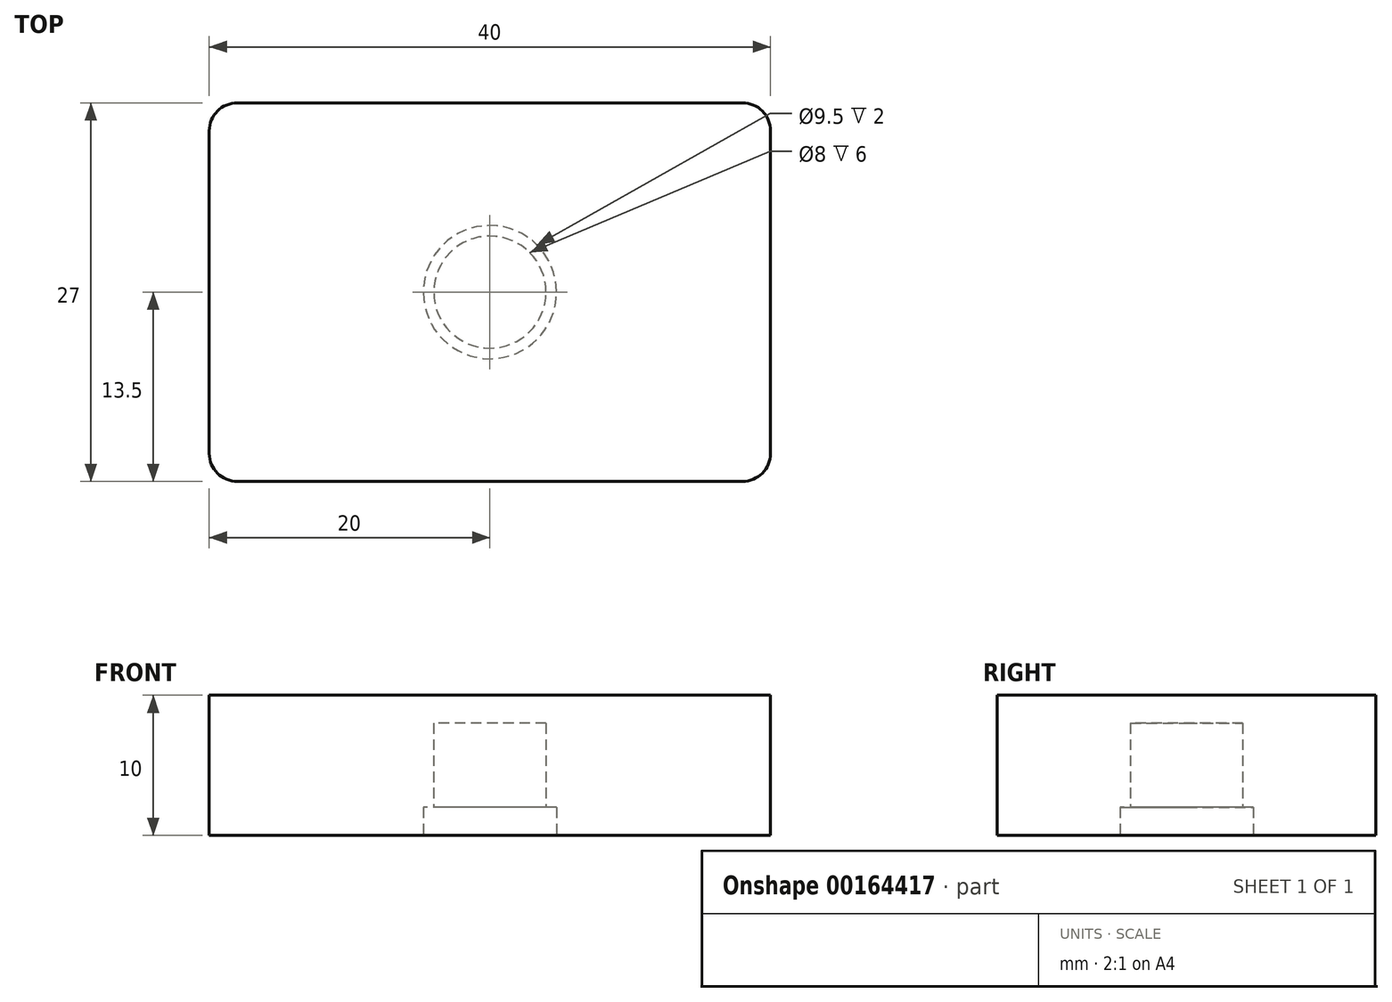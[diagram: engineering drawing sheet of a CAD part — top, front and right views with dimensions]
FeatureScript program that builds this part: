
annotation { "Feature Type Name" : "Feature", "Feature Type Description" : "" }
export const myFeature = defineFeature(function(context is Context, id is Id, definition is map)
    precondition{}
    {
        {
            var Q0;
            Q0=qCreatedBy(makeId("Top.planeOp"),FACE);
            var sketch = newSketch(context, id + "F0", { "sketchPlane" : qUnion([Q0])});
            skLineSegment(sketch, "E0.bottom", {"start": v(20, 13.5) * mm, "end": v(-20, 13.5) * mm});
            skLineSegment(sketch, "E0.top", {"start": v(20, -13.5) * mm, "end": v(-20, -13.5) * mm});
            skLineSegment(sketch, "E0.left", {"start": v(20, 13.5) * mm, "end": v(20, -13.5) * mm});
            skLineSegment(sketch, "E0.right", {"start": v(-20, 13.5) * mm, "end": v(-20, -13.5) * mm});
            skPoint(sketch, "E0.middle", {"position": v(0, 0) * mm});
            skCircle(sketch, "E1", {"center": v(0, 0) * mm, "radius": 4.75 * mm});
            skCircle(sketch, "E2", {"center": v(0, 0) * mm, "radius": 4 * mm});
            skSolve(sketch);
        }
        {
            var Q0;
            Q0=makeQuery(id+"F0.imprint","IMPRINT",FACE,{"disambiguationData":[TD([[makeQuery(id+"F0.imprint","IMPRINT",EDGE,{"derivedFrom":sQuery(id+"F0.wireOp",EDGE,"E0.bottom")}),1.0]])]});
            var Q1;
            Q1=makeQuery(id+"F0.imprint","IMPRINT",FACE,{"disambiguationData":[TD([[makeQuery(id+"F0.imprint","IMPRINT",EDGE,{"derivedFrom":sQuery(id+"F0.wireOp",EDGE,"E1")}),1.0]])]});
            var Q2;
            Q2=makeQuery(id+"F0.imprint","IMPRINT",FACE,{"disambiguationData":[TD([[makeQuery(id+"F0.imprint","IMPRINT",EDGE,{"derivedFrom":sQuery(id+"F0.wireOp",EDGE,"E2")}),1.0]])]});
            extrude(context, id + "F1", {"entities" : qUnion([Q0, Q1, Q2]), "depth" : 10 * mm});
        }
        {
            var Q0;
            Q0=makeQuery(id+"F0.imprint","IMPRINT",FACE,{"disambiguationData":[TD([[makeQuery(id+"F0.imprint","IMPRINT",EDGE,{"derivedFrom":sQuery(id+"F0.wireOp",EDGE,"E1")}),1.0]])]});
            extrude(context, id + "F2", {"entities" : qUnion([Q0]), "operationType" : NewBodyOperationType.REMOVE, "depth" : 2 * mm});
        }
        {
            var Q0;
            Q0=makeQuery(id+"F1.opExtrude","SWEPT_EDGE",EDGE,{"disambiguationData":[OSD([sQuery(id+"F0.wireOp",EDGE,"E0.top"),sQuery(id+"F0.wireOp",EDGE,"E0.left")])]});
            var Q1;
            Q1=makeQuery(id+"F1.opExtrude","SWEPT_EDGE",EDGE,{"disambiguationData":[OSD([sQuery(id+"F0.wireOp",EDGE,"E0.bottom"),sQuery(id+"F0.wireOp",EDGE,"E0.left")])]});
            var Q2;
            Q2=makeQuery(id+"F1.opExtrude","SWEPT_EDGE",EDGE,{"disambiguationData":[OSD([sQuery(id+"F0.wireOp",EDGE,"E0.bottom"),sQuery(id+"F0.wireOp",EDGE,"E0.right")])]});
            var Q3;
            Q3=makeQuery(id+"F1.opExtrude","SWEPT_EDGE",EDGE,{"disambiguationData":[OSD([sQuery(id+"F0.wireOp",EDGE,"E0.top"),sQuery(id+"F0.wireOp",EDGE,"E0.right")])]});
            fillet(context, id + "F3", {"entities" : qUnion([Q0, Q1, Q2, Q3]), "radius" : 2 * mm, "tangentPropagation" : true, "allowEdgeOverflow" : false});
        }
        {
            var Q0;
            Q0=makeQuery(id+"F2.boolean.opBoolean","SPLIT",FACE,{"disambiguationData":[TD([makeQuery(id+"F2.opExtrude","SWEPT_FACE",FACE,{"disambiguationData":[OSD([sQuery(id+"F0.wireOp",EDGE,"E2")])]})])],"derivedFrom":makeQuery(id+"F1.opExtrude","CAP_FACE",FACE,{"disambiguationData":[OSD([sQuery(id+"F0.wireOp",EDGE,"E0.bottom"),sQuery(id+"F0.wireOp",EDGE,"E0.top"),sQuery(id+"F0.wireOp",EDGE,"E0.left"),sQuery(id+"F0.wireOp",EDGE,"E0.right")])],"isStart":true})});
            extrude(context, id + "F4", {"entities" : qUnion([Q0]), "operationType" : NewBodyOperationType.REMOVE, "oppositeDirection" : true, "depth" : 8 * mm});
        }
    });
